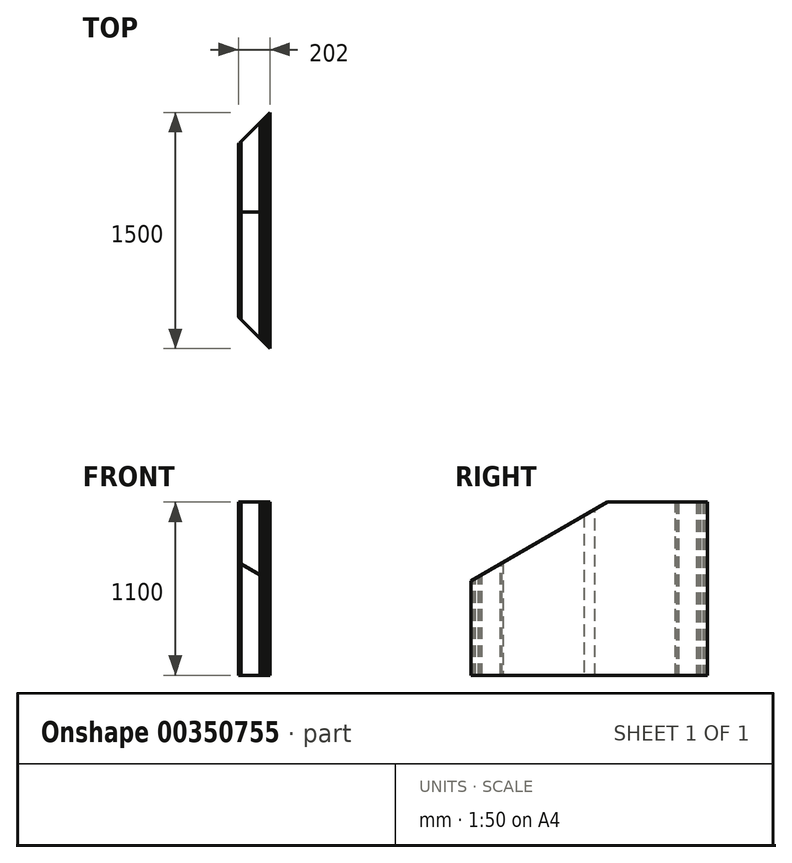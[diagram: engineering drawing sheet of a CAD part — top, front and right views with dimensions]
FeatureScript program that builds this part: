
annotation { "Feature Type Name" : "Feature", "Feature Type Description" : "" }
export const myFeature = defineFeature(function(context is Context, id is Id, definition is map)
    precondition{}
    {
        {
            var Q0;
            Q0=qCreatedBy(makeId("Right.planeOp"),FACE);
            var sketch = newSketch(context, id + "F0", { "sketchPlane" : qUnion([Q0])});
            skLineSegment(sketch, "E0", {"start": v(0, 0) * mm, "end": v(1500, 0) * mm});
            skLineSegment(sketch, "E1", {"start": v(1500, 0) * mm, "end": v(1500, 1100) * mm});
            skLineSegment(sketch, "E2", {"start": v(1500, 1100) * mm, "end": v(866.03, 1100) * mm});
            skLineSegment(sketch, "E3", {"start": v(866.03, 1100) * mm, "end": v(0, 600) * mm});
            skLineSegment(sketch, "E4", {"start": v(0, 600) * mm, "end": v(0, 0) * mm});
            skSolve(sketch);
        }
        {
            var Q0;
            Q0=makeQuery(id+"F0.imprint","IMPRINT",FACE,{"disambiguationData":[TD([[makeQuery(id+"F0.imprint","IMPRINT",EDGE,{"derivedFrom":sQuery(id+"F0.wireOp",EDGE,"E0")}),1.0]])]});
            extrude(context, id + "F1", {"entities" : qUnion([Q0]), "depth" : 6 * mm});
        }
        {
            var Q0;
            Q0=makeQuery(id+"F1.opExtrude","CAP_FACE",FACE,{"disambiguationData":[OSD([sQuery(id+"F0.wireOp",EDGE,"E0"),sQuery(id+"F0.wireOp",EDGE,"E1"),sQuery(id+"F0.wireOp",EDGE,"E2"),sQuery(id+"F0.wireOp",EDGE,"E3"),sQuery(id+"F0.wireOp",EDGE,"E4")])],"isStart":false});
            extrude(context, id + "F2", {"entities" : qUnion([Q0]), "depth" : 1 * mm});
        }
        {
            var Q0;
            Q0=makeQuery(id+"F2.opExtrude","CAP_FACE",FACE,{"disambiguationData":[OSD([sQuery(id+"F0.wireOp",EDGE,"E0"),sQuery(id+"F0.wireOp",EDGE,"E1"),sQuery(id+"F0.wireOp",EDGE,"E2"),sQuery(id+"F0.wireOp",EDGE,"E3"),sQuery(id+"F0.wireOp",EDGE,"E4")])],"isStart":false});
            extrude(context, id + "F3", {"entities" : qUnion([Q0]), "depth" : 10 * mm});
        }
        {
            var Q0;
            Q0=makeQuery(id+"F3.opExtrude","CAP_FACE",FACE,{"disambiguationData":[OSD([sQuery(id+"F0.wireOp",EDGE,"E0"),sQuery(id+"F0.wireOp",EDGE,"E1"),sQuery(id+"F0.wireOp",EDGE,"E2"),sQuery(id+"F0.wireOp",EDGE,"E3"),sQuery(id+"F0.wireOp",EDGE,"E4")])],"isStart":false});
            extrude(context, id + "F4", {"entities" : qUnion([Q0]), "depth" : 120 * mm});
        }
        {
            var Q0;
            Q0=makeQuery(id+"F4.opExtrude","CAP_FACE",FACE,{"disambiguationData":[OSD([sQuery(id+"F0.wireOp",EDGE,"E0"),sQuery(id+"F0.wireOp",EDGE,"E1"),sQuery(id+"F0.wireOp",EDGE,"E2"),sQuery(id+"F0.wireOp",EDGE,"E3"),sQuery(id+"F0.wireOp",EDGE,"E4")])],"isStart":false});
            extrude(context, id + "F5", {"entities" : qUnion([Q0]), "depth" : 10 * mm});
        }
        {
            var Q0;
            Q0=makeQuery(id+"F5.opExtrude","CAP_FACE",FACE,{"disambiguationData":[OSD([sQuery(id+"F0.wireOp",EDGE,"E0"),sQuery(id+"F0.wireOp",EDGE,"E1"),sQuery(id+"F0.wireOp",EDGE,"E2"),sQuery(id+"F0.wireOp",EDGE,"E3"),sQuery(id+"F0.wireOp",EDGE,"E4")])],"isStart":false});
            extrude(context, id + "F6", {"entities" : qUnion([Q0]), "depth" : 10 * mm});
        }
        {
            var Q0;
            Q0=makeQuery(id+"F6.opExtrude","CAP_FACE",FACE,{"disambiguationData":[OSD([sQuery(id+"F0.wireOp",EDGE,"E0"),sQuery(id+"F0.wireOp",EDGE,"E1"),sQuery(id+"F0.wireOp",EDGE,"E2"),sQuery(id+"F0.wireOp",EDGE,"E3"),sQuery(id+"F0.wireOp",EDGE,"E4")])],"isStart":false});
            extrude(context, id + "F7", {"entities" : qUnion([Q0]), "depth" : 18 * mm});
        }
        {
            var Q0;
            Q0=makeQuery(id+"F7.opExtrude","CAP_FACE",FACE,{"disambiguationData":[OSD([sQuery(id+"F0.wireOp",EDGE,"E0"),sQuery(id+"F0.wireOp",EDGE,"E1"),sQuery(id+"F0.wireOp",EDGE,"E2"),sQuery(id+"F0.wireOp",EDGE,"E3"),sQuery(id+"F0.wireOp",EDGE,"E4")])],"isStart":false});
            extrude(context, id + "F8", {"entities" : qUnion([Q0]), "depth" : 10 * mm});
        }
        {
            var Q0;
            Q0=makeQuery(id+"F8.opExtrude","CAP_FACE",FACE,{"disambiguationData":[OSD([sQuery(id+"F0.wireOp",EDGE,"E0"),sQuery(id+"F0.wireOp",EDGE,"E1"),sQuery(id+"F0.wireOp",EDGE,"E2"),sQuery(id+"F0.wireOp",EDGE,"E3"),sQuery(id+"F0.wireOp",EDGE,"E4")])],"isStart":false});
            extrude(context, id + "F9", {"entities" : qUnion([Q0]), "depth" : 1 * mm});
        }
        {
            var Q0;
            Q0=makeQuery(id+"F9.opExtrude","CAP_FACE",FACE,{"disambiguationData":[OSD([sQuery(id+"F0.wireOp",EDGE,"E0"),sQuery(id+"F0.wireOp",EDGE,"E1"),sQuery(id+"F0.wireOp",EDGE,"E2"),sQuery(id+"F0.wireOp",EDGE,"E3"),sQuery(id+"F0.wireOp",EDGE,"E4")])],"isStart":false});
            var sketch = newSketch(context, id + "F10", { "sketchPlane" : qUnion([Q0])});
            skLineSegment(sketch, "E5", {"start": v(0, 0) * mm, "end": v(70, 0) * mm});
            skLineSegment(sketch, "E6", {"start": v(70, 0) * mm, "end": v(70, 640.41) * mm});
            skLineSegment(sketch, "E7", {"start": v(70, 640.41) * mm, "end": v(0, 600) * mm});
            skLineSegment(sketch, "E8", {"start": v(0, 600) * mm, "end": v(0, 0) * mm});
            skLineSegment(sketch, "E9", {"start": v(785, 0) * mm, "end": v(785, 1053.22) * mm});
            skLineSegment(sketch, "E10", {"start": v(785, 1053.22) * mm, "end": v(715, 1012.8) * mm});
            skLineSegment(sketch, "E11", {"start": v(715, 1012.8) * mm, "end": v(715, 0) * mm});
            skLineSegment(sketch, "E12", {"start": v(715, 0) * mm, "end": v(785, 0) * mm});
            skLineSegment(sketch, "E13", {"start": v(1500, 0) * mm, "end": v(1500, 1100) * mm});
            skLineSegment(sketch, "E14", {"start": v(1500, 1100) * mm, "end": v(1430, 1100) * mm});
            skLineSegment(sketch, "E15", {"start": v(1430, 1100) * mm, "end": v(1430, 0) * mm});
            skLineSegment(sketch, "E16", {"start": v(1430, 0) * mm, "end": v(1500, 0) * mm});
            skLineSegment(sketch, "E17", {"start": v(70, 0) * mm, "end": v(715, 0) * mm, "construction": true});
            skLineSegment(sketch, "E18", {"start": v(785, 0) * mm, "end": v(1430, 0) * mm, "construction": true});
            skSolve(sketch);
        }
        {
            var Q0;
            Q0=makeQuery(id+"F10.imprint","IMPRINT",FACE,{"disambiguationData":[TD([[makeQuery(id+"F10.imprint","IMPRINT",EDGE,{"derivedFrom":sQuery(id+"F10.wireOp",EDGE,"E13")}),1.0]])]});
            var Q1;
            Q1=makeQuery(id+"F10.imprint","IMPRINT",FACE,{"disambiguationData":[TD([[makeQuery(id+"F10.imprint","IMPRINT",EDGE,{"derivedFrom":sQuery(id+"F10.wireOp",EDGE,"E9")}),1.0]])]});
            var Q2;
            Q2=makeQuery(id+"F10.imprint","IMPRINT",FACE,{"disambiguationData":[TD([[makeQuery(id+"F10.imprint","IMPRINT",EDGE,{"derivedFrom":sQuery(id+"F10.wireOp",EDGE,"E5")}),1.0]])]});
            extrude(context, id + "F11", {"entities" : qUnion([Q0, Q1, Q2]), "depth" : 8 * mm});
        }
        {
            var Q0;
            Q0=makeQuery(id+"F11.opExtrude","CAP_FACE",FACE,{"disambiguationData":[OSD([sQuery(id+"F10.wireOp",EDGE,"E9"),sQuery(id+"F10.wireOp",EDGE,"E10"),sQuery(id+"F10.wireOp",EDGE,"E11"),sQuery(id+"F10.wireOp",EDGE,"E12")])],"isStart":false});
            var sketch = newSketch(context, id + "F12", { "sketchPlane" : qUnion([Q0])});
            skLineSegment(sketch, "E19", {"start": v(0, 600) * mm, "end": v(0, 0) * mm});
            skLineSegment(sketch, "E20", {"start": v(0, 0) * mm, "end": v(1500, 0) * mm});
            skLineSegment(sketch, "E21", {"start": v(1500, 0) * mm, "end": v(1500, 1100) * mm});
            skLineSegment(sketch, "E22", {"start": v(1500, 1100) * mm, "end": v(866.03, 1100) * mm});
            skLineSegment(sketch, "E23", {"start": v(866.03, 1100) * mm, "end": v(0, 600) * mm});
            skSolve(sketch);
        }
        {
            var Q0;
            Q0 = qSketchRegion(id + "F12", true);
            extrude(context, id + "F13", {"entities" : qUnion([Q0]), "depth" : 8 * mm});
        }
        {
            var Q0;
            Q0=makeQuery(id+"F4.opExtrude","SWEPT_FACE",FACE,{"disambiguationData":[OSD([sQuery(id+"F0.wireOp",EDGE,"E2")])]});
            var sketch = newSketch(context, id + "F14", { "sketchPlane" : qUnion([Q0])});
            skLineSegment(sketch, "E24", {"start": v(202, 1500) * mm, "end": v(0, 1500) * mm});
            skLineSegment(sketch, "E25", {"start": v(0, 1500) * mm, "end": v(0, 1298) * mm});
            skLineSegment(sketch, "E26", {"start": v(0, 1298) * mm, "end": v(202, 1500) * mm});
            skSolve(sketch);
        }
        {
            var Q0;
            Q0 = qSketchRegion(id + "F14", true);
            extrude(context, id + "F15", {"entities" : qUnion([Q0]), "operationType" : NewBodyOperationType.REMOVE, "endBound" : BoundingType.THROUGH_ALL, "oppositeDirection" : true, "depth" : 25 * mm});
        }
        {
            var Q0;
            Q0=makeQuery(id+"F4.opExtrude","SWEPT_FACE",FACE,{"disambiguationData":[OSD([sQuery(id+"F0.wireOp",EDGE,"E0")])]});
            var sketch = newSketch(context, id + "F16", { "sketchPlane" : qUnion([Q0])});
            skLineSegment(sketch, "E27", {"start": v(0, -202) * mm, "end": v(202, 0) * mm});
            skLineSegment(sketch, "E28", {"start": v(202, 0) * mm, "end": v(0, 0) * mm});
            skLineSegment(sketch, "E29", {"start": v(0, 0) * mm, "end": v(0, -202) * mm});
            skSolve(sketch);
        }
        {
            var Q0;
            Q0 = qSketchRegion(id + "F16", true);
            extrude(context, id + "F17", {"entities" : qUnion([Q0]), "operationType" : NewBodyOperationType.REMOVE, "endBound" : BoundingType.THROUGH_ALL, "oppositeDirection" : true, "depth" : 25 * mm});
        }
    });
